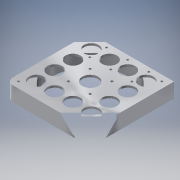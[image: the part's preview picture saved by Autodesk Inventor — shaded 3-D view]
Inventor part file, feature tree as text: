
AUTODESK INVENTOR PART (.ipt)
format: ipt  version: 2016 (Build 200138000, 138)  size: 240,128 bytes
history: native  units: mm
features: sketch x6, extrude x4, hole x2, reference x2, projected_geometry x2, thicken_offset x1
ambient origin geometry x8: Origin, YZ Plane, XZ Plane, XY Plane, X Axis, Y Axis, Z Axis, Center Point
bodies: Solid1 (feature_tree)
feature tree (17):
  extrude  "Extrusion1"  TaperAngle=0.0deg  [1 undecoded]
  extrude  "Extrusion2"  TaperAngle=0.0deg  [1 undecoded]
  extrude  "Extrusion3"  Depth=3.0mm
  hole  "Hole1"  [1 undecoded]
  thicken_offset  "Thicken1"
  hole  "Hole2"  [1 undecoded]
  extrude  "Extrusion4"  Depth=10.0mm
  sketch  "Sketch1"  dims[d0=18.0mm d1=0.0mm]
  reference  "Reference1"
  reference  "Reference2"
  sketch  "Sketch2"  dims[d2=3.0mm d3=0.0mm]
  projected_geometry  "Projected Loop1"
  sketch  "Sketch3"  dims[d4=23.0mm d5=3.0mm]
  sketch  "Sketch4"  dims[d6=0.0mm d7=31.0mm]
  sketch  "Sketch5"  dims[d8=31.0mm]
  sketch  "Sketch6"  dims[d9=3.4mm d10=6.0mm d11=4.0mm d12=2.0mm d13=90.0deg d14=8.0mm d15=20.594885mm d16=0.6mm d17=0.5mm d21=60.0mm d22=24.0mm d23=6.0mm d24=3.1mm d25=6.0mm d26=4.0mm d27=2.0mm d28=90.0deg d29=2.0mm d30=20.594885mm d32=21.0mm d37=40.0mm d39=26.0mm d40=10.0mm d42=10.0mm d44=20.0mm d46=26.0mm d47=10.0mm d49=10.0mm d51=20.0mm d53=26.0mm d54=10.0mm d56=10.0mm d59=26.0mm d60=10.0mm d61=0.0mm]
  projected_geometry  "Projected Loop2"
note: 4 required parameter values undecoded (feature->parameter linkage not recoverable at this tier; creation-order binding heuristic only, values carry confidence <= 0.55)
